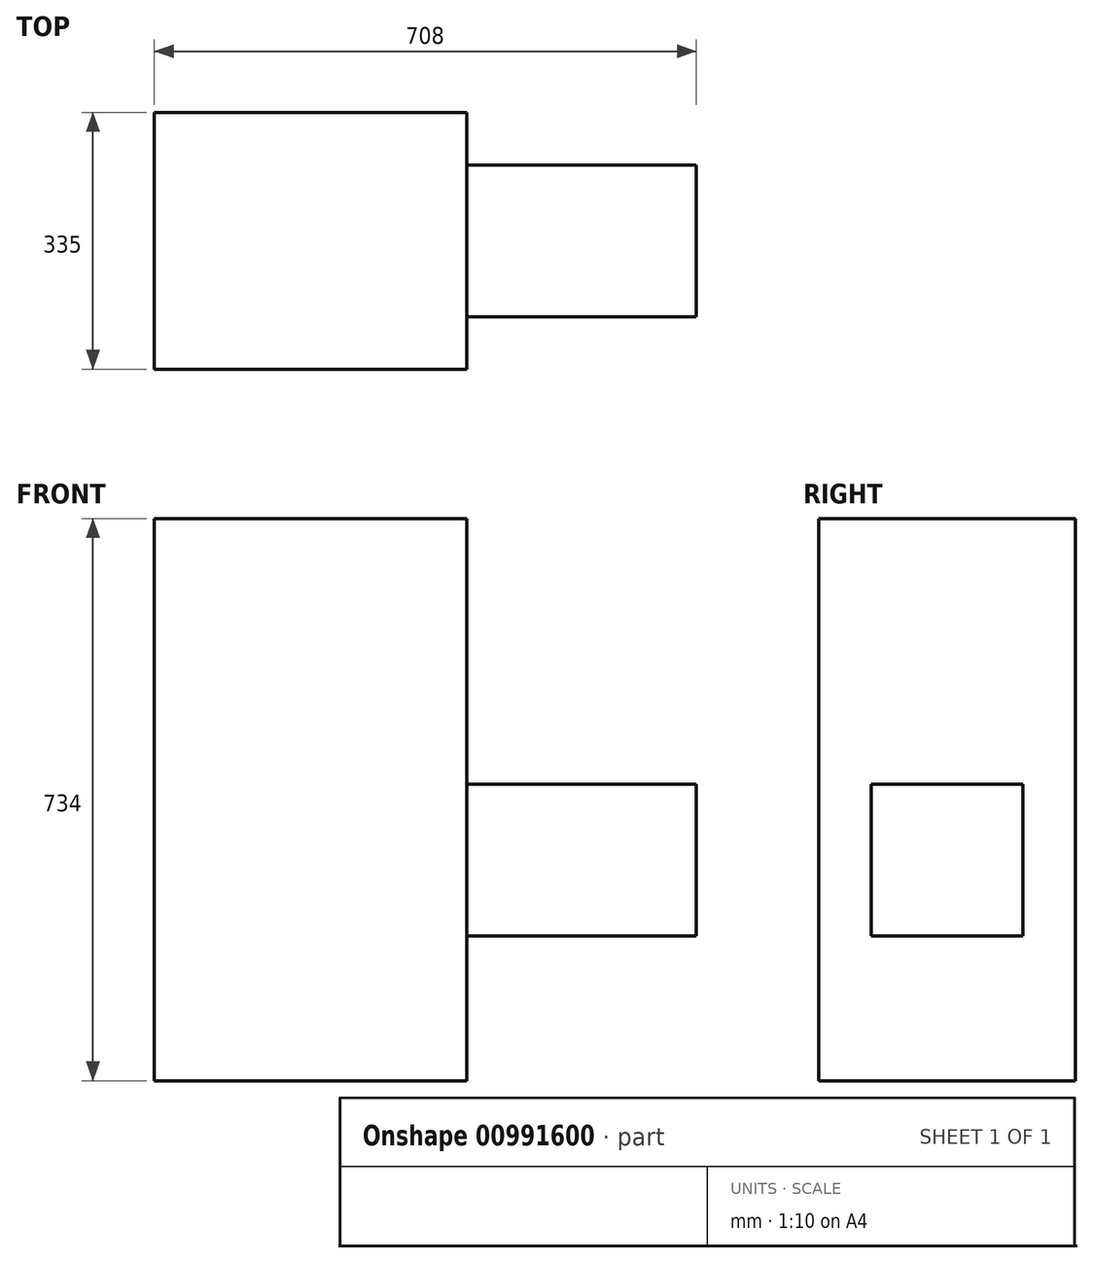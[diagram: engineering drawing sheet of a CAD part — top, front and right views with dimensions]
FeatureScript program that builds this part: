
annotation { "Feature Type Name" : "Feature", "Feature Type Description" : "" }
export const myFeature = defineFeature(function(context is Context, id is Id, definition is map)
    precondition{}
    {
        {
            var Q0;
            Q0=qCreatedBy(makeId("Right.planeOp"),FACE);
            var sketch = newSketch(context, id + "F0", { "sketchPlane" : qUnion([Q0])});
            skLineSegment(sketch, "E0.bottom", {"start": v(163.65, 734) * mm, "end": v(-171.35, 734) * mm});
            skLineSegment(sketch, "E0.top", {"start": v(163.65, 0) * mm, "end": v(-171.35, 0) * mm});
            skLineSegment(sketch, "E0.left", {"start": v(163.65, 734) * mm, "end": v(163.65, 0) * mm});
            skLineSegment(sketch, "E0.right", {"start": v(-171.35, 734) * mm, "end": v(-171.35, 0) * mm});
            skSolve(sketch);
        }
        {
            var Q0;
            Q0 = qSketchRegion(id + "F0", true);
            extrude(context, id + "F1", {"entities" : qUnion([Q0]), "oppositeDirection" : true, "depth" : 408 * mm, "offsetDistance" : 25 * mm});
        }
        {
            var Q0;
            Q0=makeQuery(id+"F1.opExtrude","CAP_FACE",FACE,{"disambiguationData":[OSD([sQuery(id+"F0.wireOp",EDGE,"E0.bottom"),sQuery(id+"F0.wireOp",EDGE,"E0.top"),sQuery(id+"F0.wireOp",EDGE,"E0.left"),sQuery(id+"F0.wireOp",EDGE,"E0.right")])],"isStart":true});
            var sketch = newSketch(context, id + "F2", { "sketchPlane" : qUnion([Q0])});
            skLineSegment(sketch, "E1.bottom", {"start": v(-102.85, 387) * mm, "end": v(95.15, 387) * mm});
            skLineSegment(sketch, "E1.top", {"start": v(-102.85, 189) * mm, "end": v(95.15, 189) * mm});
            skLineSegment(sketch, "E1.left", {"start": v(-102.85, 387) * mm, "end": v(-102.85, 189) * mm});
            skLineSegment(sketch, "E1.right", {"start": v(95.15, 387) * mm, "end": v(95.15, 189) * mm});
            skSolve(sketch);
        }
        {
            var Q0;
            Q0 = qSketchRegion(id + "F2", true);
            extrude(context, id + "F3", {"entities" : qUnion([Q0]), "operationType" : NewBodyOperationType.ADD, "depth" : 300 * mm, "offsetDistance" : 25 * mm});
        }
    });
